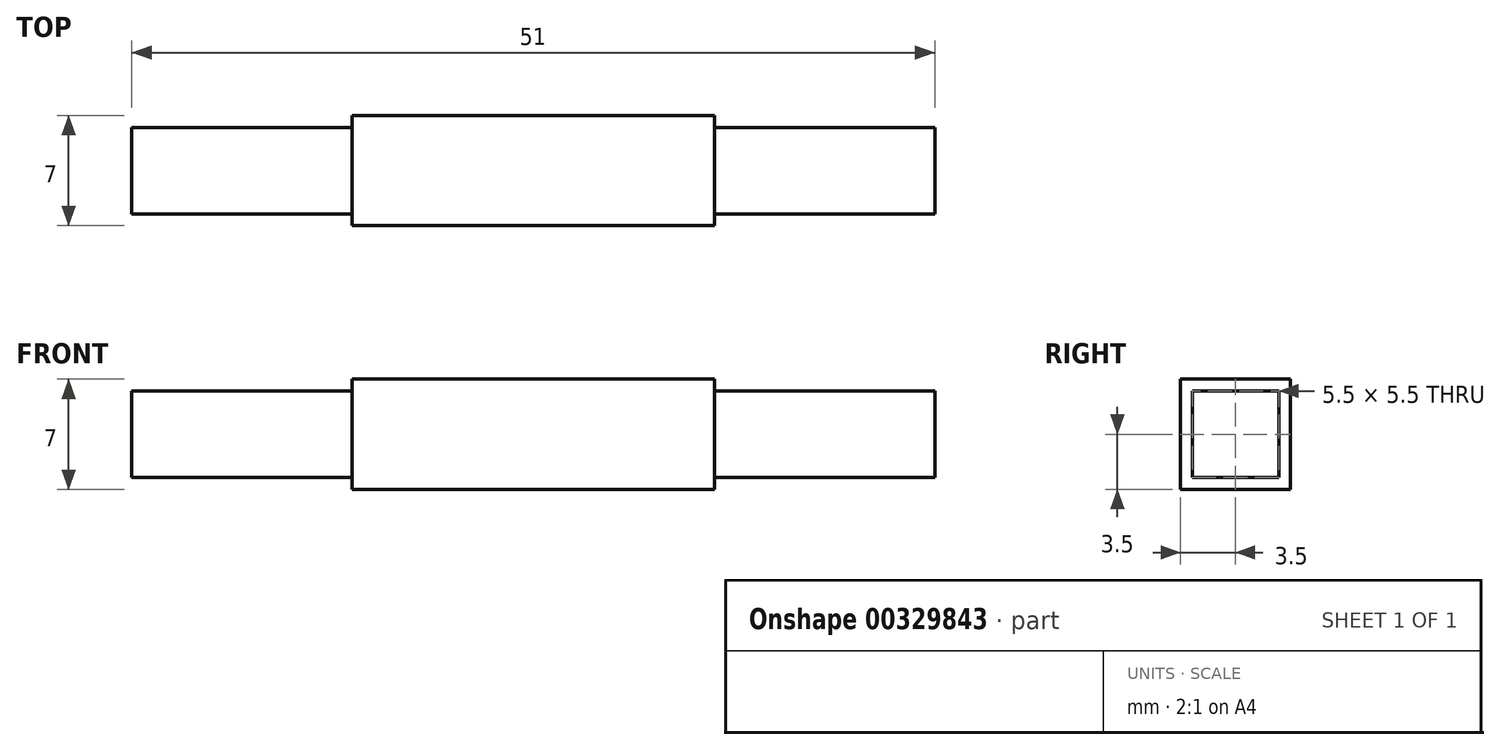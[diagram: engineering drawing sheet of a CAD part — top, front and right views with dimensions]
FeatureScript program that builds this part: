
annotation { "Feature Type Name" : "Feature", "Feature Type Description" : "" }
export const myFeature = defineFeature(function(context is Context, id is Id, definition is map)
    precondition{}
    {
        {
            var Q0;
            Q0=qCreatedBy(makeId("Right.planeOp"),FACE);
            var sketch = newSketch(context, id + "F0", { "sketchPlane" : qUnion([Q0])});
            skLineSegment(sketch, "E0.bottom", {"start": v(0, 0) * mm, "end": v(7, 0) * mm});
            skLineSegment(sketch, "E0.top", {"start": v(0, 7) * mm, "end": v(7, 7) * mm});
            skLineSegment(sketch, "E0.left", {"start": v(0, 0) * mm, "end": v(0, 7) * mm});
            skLineSegment(sketch, "E0.right", {"start": v(7, 0) * mm, "end": v(7, 7) * mm});
            skSolve(sketch);
        }
        {
            var Q0;
            Q0=makeQuery(id+"F0.imprint","IMPRINT",FACE,{"disambiguationData":[TD([[makeQuery(id+"F0.imprint","IMPRINT",EDGE,{"derivedFrom":sQuery(id+"F0.wireOp",EDGE,"E0.bottom")}),1.0]])]});
            extrude(context, id + "F1", {"entities" : qUnion([Q0]), "depth" : 11.5 * mm, "offsetDistance" : 25 * mm});
        }
        {
            var Q0;
            Q0=makeQuery(id+"F1.opExtrude","CAP_FACE",FACE,{"disambiguationData":[OSD([sQuery(id+"F0.wireOp",EDGE,"E0.bottom"),sQuery(id+"F0.wireOp",EDGE,"E0.top"),sQuery(id+"F0.wireOp",EDGE,"E0.left"),sQuery(id+"F0.wireOp",EDGE,"E0.right")])],"isStart":false});
            var sketch = newSketch(context, id + "F2", { "sketchPlane" : qUnion([Q0])});
            skLineSegment(sketch, "E1.bottom", {"start": v(0.75, 0.75) * mm, "end": v(6.25, 0.75) * mm});
            skLineSegment(sketch, "E1.top", {"start": v(0.75, 6.25) * mm, "end": v(6.25, 6.25) * mm});
            skLineSegment(sketch, "E1.left", {"start": v(0.75, 0.75) * mm, "end": v(0.75, 6.25) * mm});
            skLineSegment(sketch, "E1.right", {"start": v(6.25, 0.75) * mm, "end": v(6.25, 6.25) * mm});
            skPoint(sketch, "E1.middle", {"position": v(3.5, 3.5) * mm});
            skLineSegment(sketch, "E2", {"start": v(0, 3.5) * mm, "end": v(3.5, 3.5) * mm, "construction": true});
            skLineSegment(sketch, "E3", {"start": v(3.5, 3.5) * mm, "end": v(3.5, 0) * mm, "construction": true});
            skSolve(sketch);
        }
        {
            var Q0;
            Q0 = qSketchRegion(id + "F2", true);
            extrude(context, id + "F3", {"entities" : qUnion([Q0]), "operationType" : NewBodyOperationType.ADD, "depth" : 14 * mm, "offsetDistance" : 25 * mm});
        }
        {
            var Q0;
            Q0=makeQuery(id+"F1.opExtrude","SWEPT_BODY",BODY,{"disambiguationData":[OSD([sQuery(id+"F0.wireOp",EDGE,"E0.bottom"),sQuery(id+"F0.wireOp",EDGE,"E0.top"),sQuery(id+"F0.wireOp",EDGE,"E0.left"),sQuery(id+"F0.wireOp",EDGE,"E0.right")])]});
            var Q1;
            Q1=makeQuery(id+"F1.opExtrude","CAP_FACE",FACE,{"disambiguationData":[OSD([sQuery(id+"F0.wireOp",EDGE,"E0.bottom"),sQuery(id+"F0.wireOp",EDGE,"E0.top"),sQuery(id+"F0.wireOp",EDGE,"E0.left"),sQuery(id+"F0.wireOp",EDGE,"E0.right")])],"isStart":true});
            mirror(context, id + "F4", {"operationType" : NewBodyOperationType.ADD, "entities" : qUnion([Q0]), "mirrorPlane" : qUnion([Q1])});
        }
    });
